# Revit family: STH20020_27_30_40
name_source: partatom
category: Luminárias
units: mm (PartAtom-declared; Revit-internal decimal feet)

## family parameters
Com base no plano de trabalho = Não
Compartilhado = Não
Corte com vazios quando carregada = Não
Cota do conector redondo = Utilizar diâmetro
Fonte luminosa = Sim
Manter orientação da anotação = Não
Ponto de cálculo do ambiente = Não
Sempre na vertical = Sim
Tipo de parte = Normal

## types (3) — shared parameters
Altura = 0.09 m
Cromado = Cromado
Dimerização = Não dimerizável
Diâmetro = 0.06 m
Estrutura = Al - Branco
Fabricante = Stella
Filtro de cor = 16777215
Grau de proteção (IP) = IP20
IRC (Índice de reprodução de cores) = >95 (R9 >80)
Modelo = Par20 EVO
Potência = 6 W
Tensão Elétrica = 100V-240V
Troca de temperatura da cor de lâmpada com esmaecimento = <Nenhum>
URL = https://stella.com.br
Vidro = Vidro
Ângulo de Abertura = 25°
Ângulo de inclinação = 90.00°
zero-valued in all types: Elevação padrão

## per-type parameters (varying)
| type | Arquivo de rede fotométrica | Fluxo Luminoso | Luminoso | Referência | Temperatura da cor (K) |
| STH20020/27 - BIVOLT - 2700K - 450lm - 25° | STELLA - STH20020-27 - PAR20 EVO 5,5W.ies | 450 lm | Luminoso - 2700K | STH20020/27 - BIVOLT | 2700 K |
| STH20020/30 - BIVOLT - 3000K - 450lm - 25° | STELLA - STH20020-30 - PAR20 EVO 5,5W.ies | 450 lm | Luminoso - 3000K | STH20020/30 - BIVOLT | 3000 K |
| STH20020/40 - BIVOLT - 4000K - 475lm - 25° | STELLA - STH20020-40 - PAR20 EVO 5,5W.ies | 475 lm | Luminoso - 4000K | STH20020/40 - BIVOLT | 4000 K |
